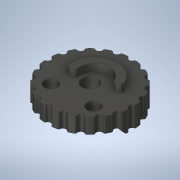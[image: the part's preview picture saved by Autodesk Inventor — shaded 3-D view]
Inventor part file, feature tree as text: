
AUTODESK INVENTOR PART (.ipt)
format: ipt  version: 2020.1 (Build 241239000, 239)  size: 350,208 bytes
history: native  units: mm
features: extrude x6, sketch x2, fillet x1, chamfer x1
ambient origin geometry x8: Origin, YZ Plane, XZ Plane, XY Plane, X Axis, Y Axis, Z Axis, Center Point
bodies: Solid1 (feature_tree)
feature tree (10):
  extrude  "Extrusion1"  Depth=1.25mm
  fillet  "Fillet1"  Radius=8.0mm
  sketch  "Sketch2"  dims[d10=6.3mm d11=12.0mm d12=7.0mm d14=2.0mm d15=0.0mm d16=2.0mm d17=0.0mm d18=0.5mm d19=15.0deg d22=5.1mm d23=5.1mm d25=8.726646mm d26=1.5mm d27=9.0mm d28=6.0mm d29=7.330383mm d30=11.5mm d31=11.0mm d32=1.0mm d33=1.5mm d34=1.5mm d35=3.0mm d36=0.0mm d37=5.0mm d38=0.0mm d39=5.0mm d40=0.0mm d41=9.599311mm d43=180.0deg d44=0.0mm d45=2.0mm d46=2.0mm d47=45.0deg]
  extrude  "Extrusion2"  Depth=2.0mm
  extrude  "Extrusion3"  Depth=2.0mm
  chamfer  "Chamfer1"  Distance=2.0mm
  extrude  "Extrusion4"  Depth=2.0mm TaperAngle=0.0deg
  extrude  "Extrusion5"  Depth=0.5mm
  extrude  "Extrusion6"  TaperAngle=15.0deg  [1 undecoded]
  sketch  "Sketch1"  dims[d1=200.0mm d2=31.0mm d3=360.0deg d6=1.25mm d7=1.25mm d8=8.0mm d9=0.0mm]
note: 1 required parameter value undecoded (feature->parameter linkage not recoverable at this tier; creation-order binding heuristic only, values carry confidence <= 0.55)
